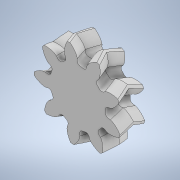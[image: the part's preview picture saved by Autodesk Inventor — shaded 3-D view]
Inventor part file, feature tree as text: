
AUTODESK INVENTOR PART (.ipt)
format: ipt  version: 2022 (Build 260153070, 153G)  size: 551,936 bytes
history: native  units: mm
features: sketch x1, extrude x1, helix x1, pattern_circular x1, mirror x1
ambient origin geometry x8: Origin, YZ Plane, XZ Plane, XY Plane, X Axis, Y Axis, Z Axis, Center Point
bodies: Solid1 (feature_tree)
feature tree (5):
  sketch  "Sketch1"  dims[d0=1.5mm d1=0.0mm d2=70.268674mm d3=1.5mm d4=10.0mm d5=0.0mm d6=90.0deg d7=90.0deg d8=0.0mm d9=0.0mm d10=90.0mm d11=360.0deg]
  extrude  "Extrusion1"  TaperAngle=0.0deg  [1 undecoded]
  helix  "Coil1"  [1 undecoded]
  pattern_circular  "Circular Pattern1"  [2 undecoded]
  mirror  "Mirror1"
note: 4 required parameter values undecoded (feature->parameter linkage not recoverable at this tier; creation-order binding heuristic only, values carry confidence <= 0.55)
